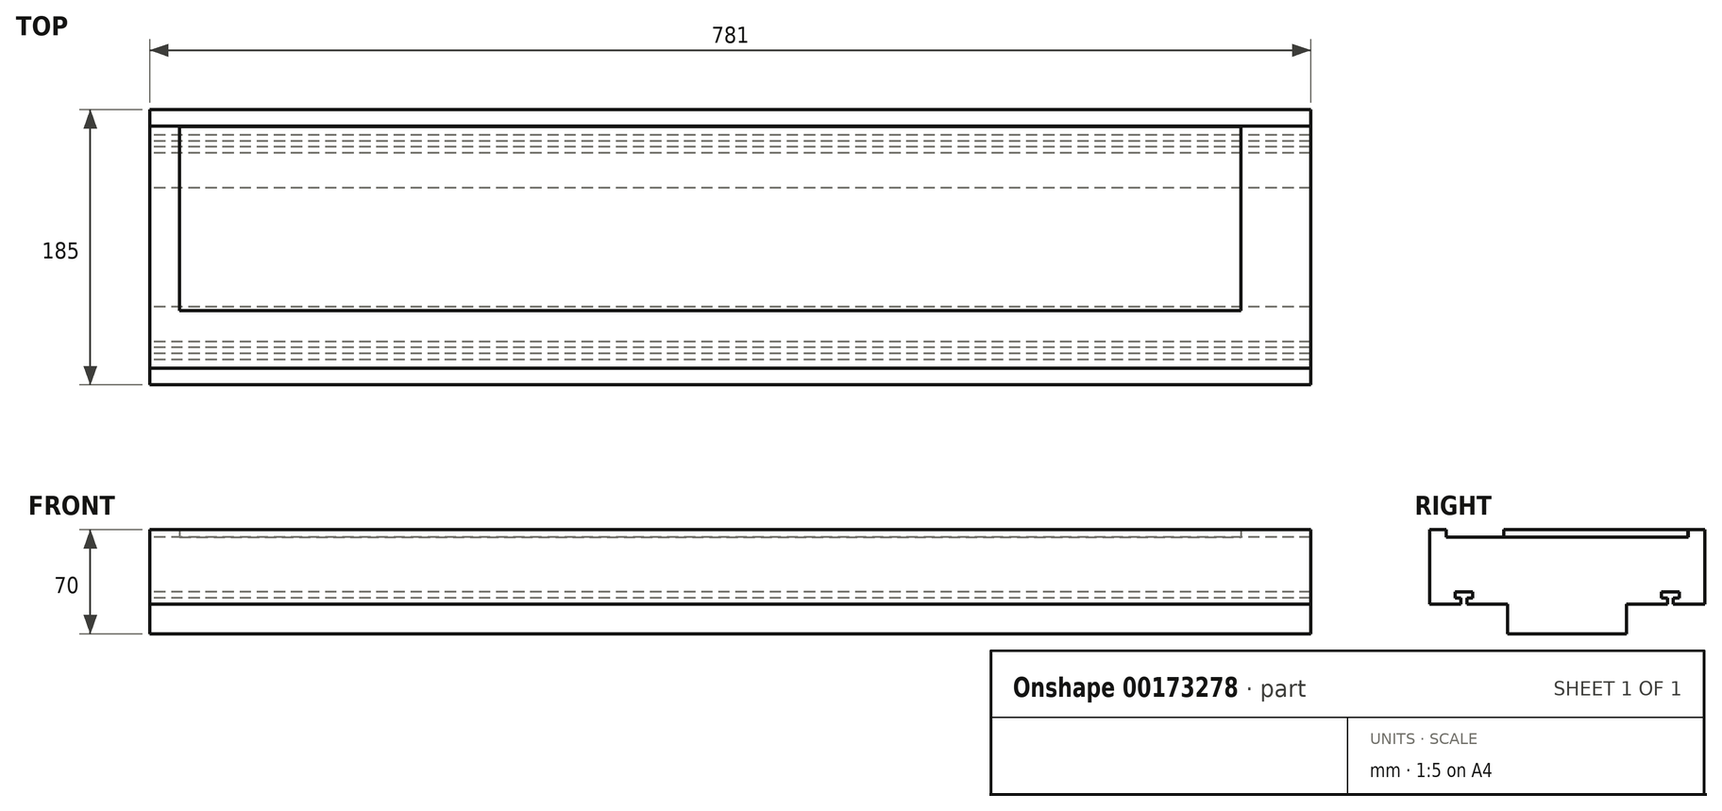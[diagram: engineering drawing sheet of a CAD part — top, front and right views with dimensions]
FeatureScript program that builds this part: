
annotation { "Feature Type Name" : "Feature", "Feature Type Description" : "" }
export const myFeature = defineFeature(function(context is Context, id is Id, definition is map)
    precondition{}
    {
        {
            var Q0;
            Q0=qCreatedBy(makeId("Right.planeOp"),FACE);
            var sketch = newSketch(context, id + "F0", { "sketchPlane" : qUnion([Q0])});
            skLineSegment(sketch, "E0", {"start": v(-92.5, 0) * mm, "end": v(92.5, 0) * mm, "construction": true});
            skLineSegment(sketch, "E1.bottom", {"start": v(-92.5, 0) * mm, "end": v(-71.5, 0) * mm});
            skLineSegment(sketch, "E1.top", {"start": v(-92.5, 50) * mm, "end": v(92.5, 50) * mm});
            skLineSegment(sketch, "E1.left", {"start": v(-92.5, 0) * mm, "end": v(-92.5, 50) * mm});
            skLineSegment(sketch, "E1.right", {"start": v(92.5, 0) * mm, "end": v(92.5, 50) * mm});
            skLineSegment(sketch, "E2", {"start": v(0, 0) * mm, "end": v(0, -20) * mm, "construction": true});
            skLineSegment(sketch, "E3", {"start": v(0, -20) * mm, "end": v(-40, -20) * mm, "construction": true});
            skLineSegment(sketch, "E4.bottom", {"start": v(-40, -20) * mm, "end": v(40, -20) * mm});
            skLineSegment(sketch, "E4.top", {"start": v(-40, 0) * mm, "end": v(40, 0) * mm});
            skLineSegment(sketch, "E4.left", {"start": v(-40, -20) * mm, "end": v(-40, 0) * mm});
            skLineSegment(sketch, "E4.right", {"start": v(40, -20) * mm, "end": v(40, 0) * mm});
            skLineSegment(sketch, "E5", {"start": v(0, 85.73) * mm, "end": v(0, -82.56) * mm, "construction": true});
            skLineSegment(sketch, "E6.0", {"start": v(-67.5, 85.73) * mm, "end": v(-67.5, 50) * mm, "construction": true});
            skLineSegment(sketch, "E7.0", {"start": v(-71.5, 85.73) * mm, "end": v(-71.5, 50) * mm, "construction": true});
            skLineSegment(sketch, "E8.0", {"start": v(-63.5, 85.73) * mm, "end": v(-63.5, 50) * mm, "construction": true});
            skLineSegment(sketch, "E9.0", {"start": v(-75.5, 4) * mm, "end": v(-71.5, 4) * mm});
            skLineSegment(sketch, "E10.0", {"start": v(-75.5, 85.73) * mm, "end": v(-75.5, 50) * mm, "construction": true});
            skLineSegment(sketch, "E11.0", {"start": v(-75.5, 8) * mm, "end": v(-63.5, 8) * mm});
            skLineSegment(sketch, "E12.trimOffspring", {"start": v(0, 8) * mm, "end": v(92.5, 8) * mm, "construction": true});
            skLineSegment(sketch, "E13.trimOffspring", {"start": v(0, 4) * mm, "end": v(92.5, 4) * mm, "construction": true});
            skLineSegment(sketch, "E14.trimOffspring", {"start": v(-63.5, 8) * mm, "end": v(-63.5, 4) * mm, "construction": true});
            skLineSegment(sketch, "E15.trimOffspring", {"start": v(-67.5, 4) * mm, "end": v(-67.5, -82.56) * mm, "construction": true});
            skLineSegment(sketch, "E16.trimOffspring", {"start": v(-71.5, 4) * mm, "end": v(-71.5, -82.56) * mm, "construction": true});
            skLineSegment(sketch, "E17.trimOffspring", {"start": v(-75.5, 8) * mm, "end": v(-75.5, 4) * mm, "construction": true});
            skLineSegment(sketch, "E18.trimOffspring", {"start": v(-75.5, 0) * mm, "end": v(-75.5, -82.56) * mm, "construction": true});
            skLineSegment(sketch, "E19.trimOffspring", {"start": v(-63.5, 0) * mm, "end": v(-63.5, -82.56) * mm, "construction": true});
            skLineSegment(sketch, "E20.trimOffspring", {"start": v(-67.5, 4) * mm, "end": v(-63.5, 4) * mm});
            skLineSegment(sketch, "E21.trimOffspring", {"start": v(-67.5, 0) * mm, "end": v(67.5, 0) * mm});
            skLineSegment(sketch, "E22", {"start": v(-71.5, 0) * mm, "end": v(-71.5, 4) * mm});
            skLineSegment(sketch, "E23", {"start": v(-75.5, 4) * mm, "end": v(-75.5, 8) * mm});
            skLineSegment(sketch, "E24", {"start": v(-63.5, 8) * mm, "end": v(-63.5, 4) * mm});
            skLineSegment(sketch, "E25", {"start": v(-67.5, 4) * mm, "end": v(-67.5, 0) * mm});
            skLineSegment(sketch, "E26.MirrorCS", {"start": v(67.5, 4) * mm, "end": v(63.5, 4) * mm});
            skLineSegment(sketch, "E27.MirrorCS", {"start": v(75.5, 4) * mm, "end": v(71.5, 4) * mm});
            skLineSegment(sketch, "E28.MirrorCS", {"start": v(67.5, 4) * mm, "end": v(67.5, 0) * mm});
            skLineSegment(sketch, "E29.MirrorCS", {"start": v(63.5, 8) * mm, "end": v(63.5, 4) * mm, "construction": true});
            skLineSegment(sketch, "E30.MirrorCS", {"start": v(75.5, 8) * mm, "end": v(75.5, 4) * mm, "construction": true});
            skLineSegment(sketch, "E31.MirrorCS", {"start": v(75.5, 4) * mm, "end": v(75.5, 8) * mm});
            skLineSegment(sketch, "E32.MirrorCS", {"start": v(71.5, 0) * mm, "end": v(71.5, 4) * mm});
            skLineSegment(sketch, "E33.MirrorCS", {"start": v(63.5, 8) * mm, "end": v(63.5, 4) * mm});
            skLineSegment(sketch, "E34.MirrorCS", {"start": v(75.5, 8) * mm, "end": v(63.5, 8) * mm});
            skLineSegment(sketch, "E35.trimOffspring", {"start": v(71.5, 0) * mm, "end": v(92.5, 0) * mm});
            skSolve(sketch);
        }
        {
            var Q0;
            Q0=qSketchRegion(id+"F0",true);
            extrude(context, id + "F1", {"entities" : qUnion([Q0]), "endBound" : BoundingType.SYMMETRIC, "depth" : 781 * mm});
        }
        {
            var Q0;
            Q0=makeQuery(id+"F1.opExtrude","SWEPT_FACE",FACE,{"disambiguationData":[OSD([sQuery(id+"F0.wireOp",EDGE,"E1.top")])]});
            var sketch = newSketch(context, id + "F2", { "sketchPlane" : qUnion([Q0])});
            skLineSegment(sketch, "E36.0", {"start": v(390.5, 81.5) * mm, "end": v(-390.5, 81.5) * mm});
            skLineSegment(sketch, "E37.0", {"start": v(390.5, -81.5) * mm, "end": v(-390.5, -81.5) * mm});
            skLineSegment(sketch, "E38.0", {"start": v(-390.5, -92.5) * mm, "end": v(-390.5, 92.5) * mm});
            skLineSegment(sketch, "E39.0", {"start": v(390.5, -92.5) * mm, "end": v(390.5, 92.5) * mm});
            skSolve(sketch);
        }
        {
            var Q0;
            Q0=qSketchRegion(id+"F2",true);
            extrude(context, id + "F3", {"entities" : qUnion([Q0]), "operationType" : NewBodyOperationType.REMOVE, "oppositeDirection" : true, "depth" : 5 * mm});
        }
        {
            var Q0;
            Q0=makeQuery(id+"F3.boolean.opBoolean","COPY",FACE,{"derivedFrom":makeQuery(id+"F3.opExtrude","CAP_FACE",FACE,{"disambiguationData":[OSD([sQuery(id+"F2.wireOp",EDGE,"E36.0"),sQuery(id+"F2.wireOp",EDGE,"E37.0"),sQuery(id+"F2.wireOp",EDGE,"E38.0"),sQuery(id+"F2.wireOp",EDGE,"E39.0")])],"isStart":false})});
            var sketch = newSketch(context, id + "F4", { "sketchPlane" : qUnion([Q0])});
            skLineSegment(sketch, "E40.bottom", {"start": v(-370.5, 81.3) * mm, "end": v(343.5, 81.3) * mm});
            skLineSegment(sketch, "E40.top", {"start": v(-370.5, -42.7) * mm, "end": v(343.5, -42.7) * mm});
            skLineSegment(sketch, "E40.left", {"start": v(-370.5, 81.3) * mm, "end": v(-370.5, -42.7) * mm});
            skLineSegment(sketch, "E40.right", {"start": v(343.5, 81.3) * mm, "end": v(343.5, -42.7) * mm});
            skSolve(sketch);
        }
        {
            var Q0;
            Q0=qSketchRegion(id+"F4",true);
            extrude(context, id + "F5", {"entities" : qUnion([Q0]), "operationType" : NewBodyOperationType.ADD, "depth" : 5 * mm});
        }
    });
